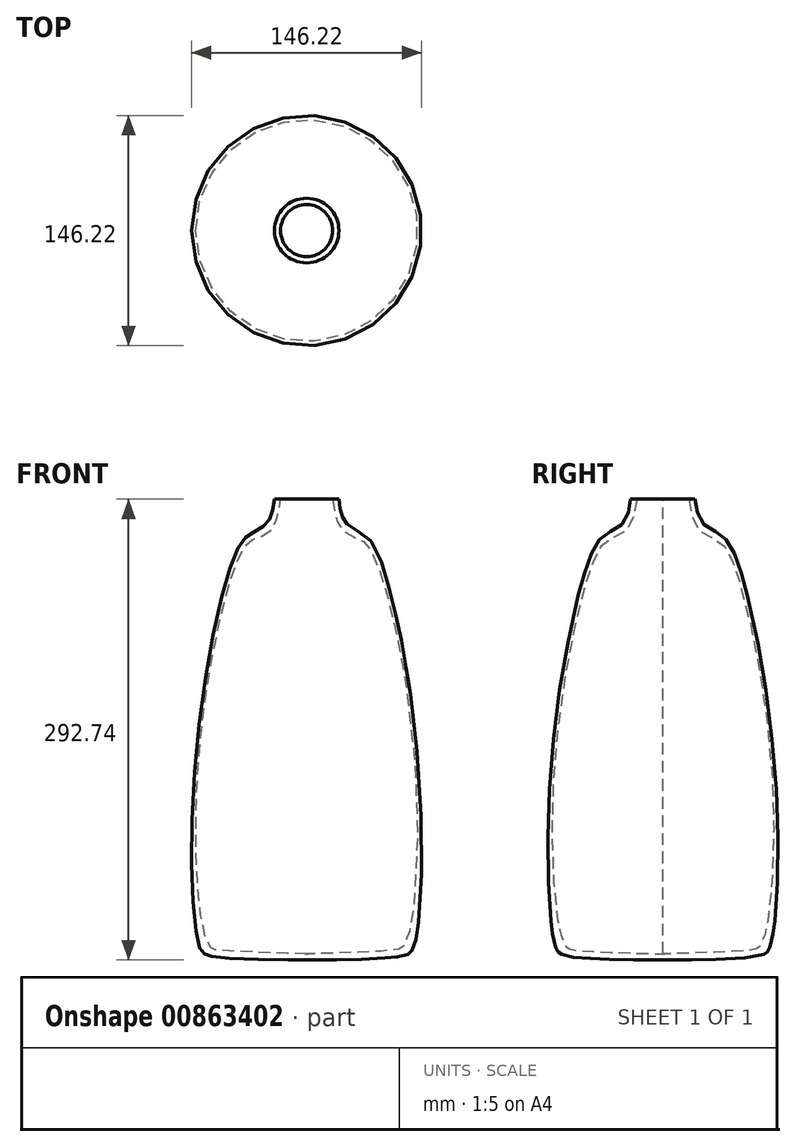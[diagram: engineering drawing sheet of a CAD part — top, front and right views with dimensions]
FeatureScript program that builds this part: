
annotation { "Feature Type Name" : "Feature", "Feature Type Description" : "" }
export const myFeature = defineFeature(function(context is Context, id is Id, definition is map)
    precondition{}
    {
        {
            var Q0;
            Q0=qCreatedBy(makeId("Front.planeOp"),FACE);
            var sketch = newSketch(context, id + "F0", { "sketchPlane" : qUnion([Q0])});
            skLineSegment(sketch, "E0.right", {"start": v(75, 0) * mm, "end": v(75, 300) * mm});
            skFitSpline(sketch, "E1", {"points": [v(75, 3.58) * mm, v(17.82, 5.4) * mm, v(10.26, 7.45) * mm, v(7.05, 11.32) * mm, v(9.26, 127.88) * mm, v(30.3, 263.2) * mm, v(39.2, 274.24) * mm, v(47.9, 279.27) * mm, v(52.36, 285.66) * mm, v(54.48, 296.3) * mm], "startDerivative": vector(-144.07, -2.7) * mm, "endDerivative": vector(13.26, 194.17) * mm});
            skFitSpline(sketch, "E2", {"points": [v(196.48, 3.58) * mm, v(139.3, 5.4) * mm, v(131.74, 7.45) * mm, v(128.53, 11.32) * mm, v(125.57, 128.21) * mm, v(151.78, 263.2) * mm, v(160.68, 274.24) * mm, v(169.39, 279.27) * mm, v(173.84, 285.66) * mm, v(175.97, 296.3) * mm], "startDerivative": vector(-144.07, -2.7) * mm, "endDerivative": vector(13.26, 194.17) * mm});
            skFitSpline(sketch, "E3", {"points": [v(196.48, 7.58) * mm, v(139.75, 9.89) * mm, v(137.59, 10.43) * mm, v(134.22, 13.24) * mm, v(127.57, 127.88) * mm, v(154.55, 262.06) * mm, v(162.8, 270.85) * mm, v(172.2, 275.14) * mm, v(177.57, 284.23) * mm, v(179.97, 296.3) * mm], "startDerivative": vector(-144.07, -2.7) * mm, "endDerivative": vector(13.26, 194.17) * mm});
            skLineSegment(sketch, "E4", {"start": v(175.97, 296.3) * mm, "end": v(179.97, 296.3) * mm});
            skLineSegment(sketch, "E5", {"start": v(196.48, 3.58) * mm, "end": v(196.48, 7.58) * mm});
            skSolve(sketch);
        }
        {
            var Q0;
            Q0=makeQuery(id+"F0.imprint","IMPRINT",FACE,{"disambiguationData":[TD([[makeQuery(id+"F0.imprint","IMPRINT",EDGE,{"derivedFrom":sQuery(id+"F0.wireOp",EDGE,"E2")}),-1.0]])]});
            var Q1;
            Q1=sQuery(id+"F0.wireOp",EDGE,"E5");
            revolve(context, id + "F1", {"surfaceOperationType" : NewSurfaceOperationType.NEW, "entities" : qUnion([Q0]), "axis" : qUnion([Q1]), "revolveType" : RevolveType.TWO_DIRECTIONS, "oppositeDirection" : true, "angle" : 120 * degree, "angleBack" : 120 * degree});
        }
    });
